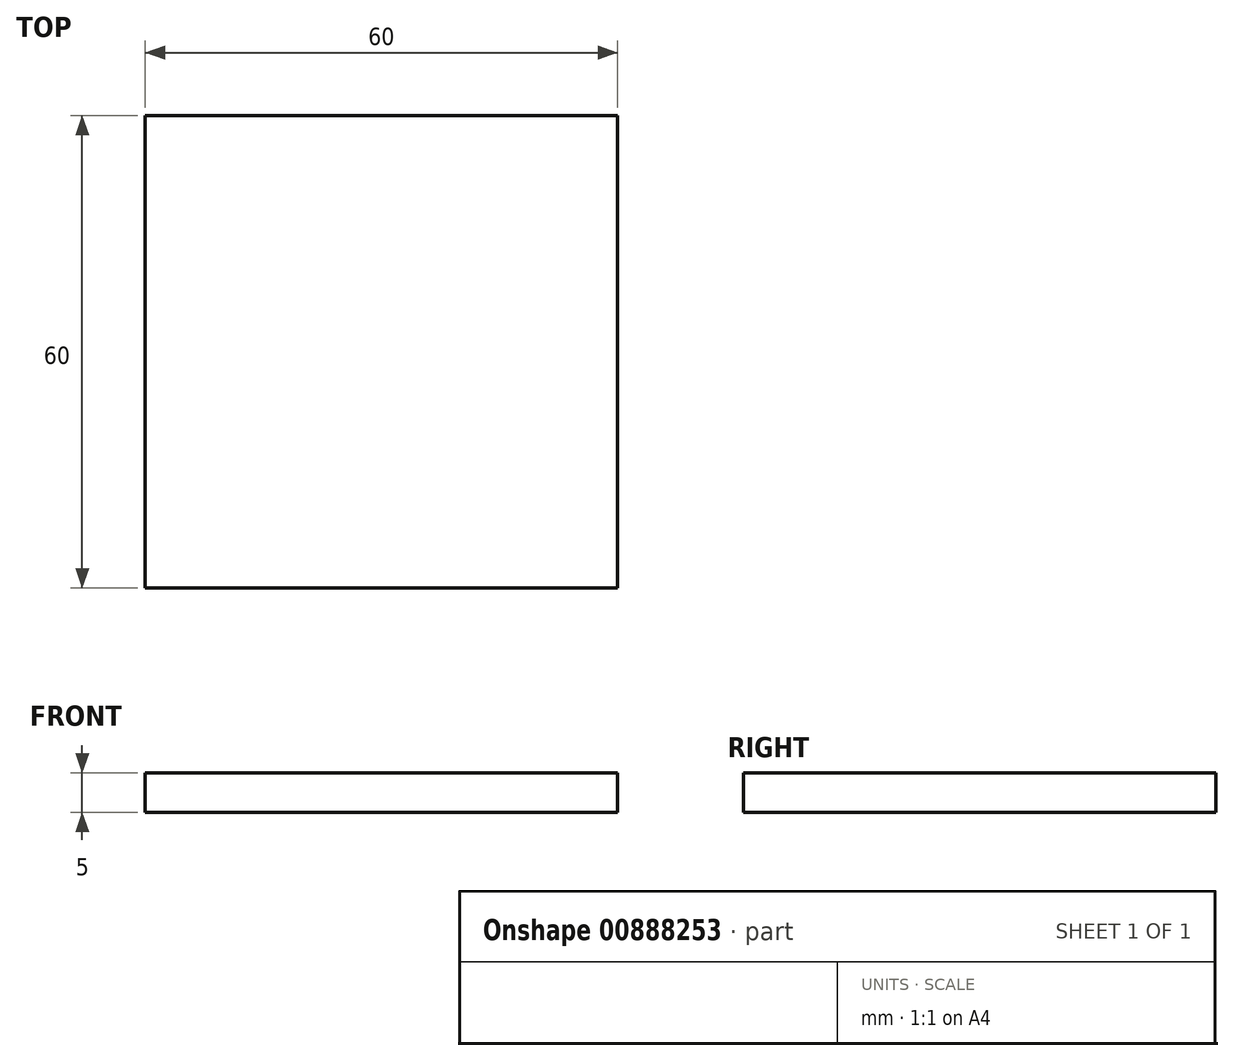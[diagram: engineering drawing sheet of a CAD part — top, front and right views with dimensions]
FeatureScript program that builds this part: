
annotation { "Feature Type Name" : "Feature", "Feature Type Description" : "" }
export const myFeature = defineFeature(function(context is Context, id is Id, definition is map)
    precondition{}
    {
        {
            var Q0;
            Q0=qCreatedBy(makeId("Top.planeOp"),FACE);
            var sketch = newSketch(context, id + "F0", { "sketchPlane" : qUnion([Q0])});
            skLineSegment(sketch, "E0.bottom", {"start": v(-30, 30) * mm, "end": v(30, 30) * mm});
            skLineSegment(sketch, "E0.top", {"start": v(-30, -30) * mm, "end": v(30, -30) * mm});
            skLineSegment(sketch, "E0.left", {"start": v(-30, 30) * mm, "end": v(-30, -30) * mm});
            skLineSegment(sketch, "E0.right", {"start": v(30, 30) * mm, "end": v(30, -30) * mm});
            skPoint(sketch, "E0.middle", {"position": v(0, 0) * mm});
            skSolve(sketch);
        }
        {
            var Q0;
            Q0 = qSketchRegion(id + "F0", true);
            extrude(context, id + "F1", {"entities" : qUnion([Q0]), "depth" : 5 * mm, "offsetDistance" : 25 * mm});
        }
    });
